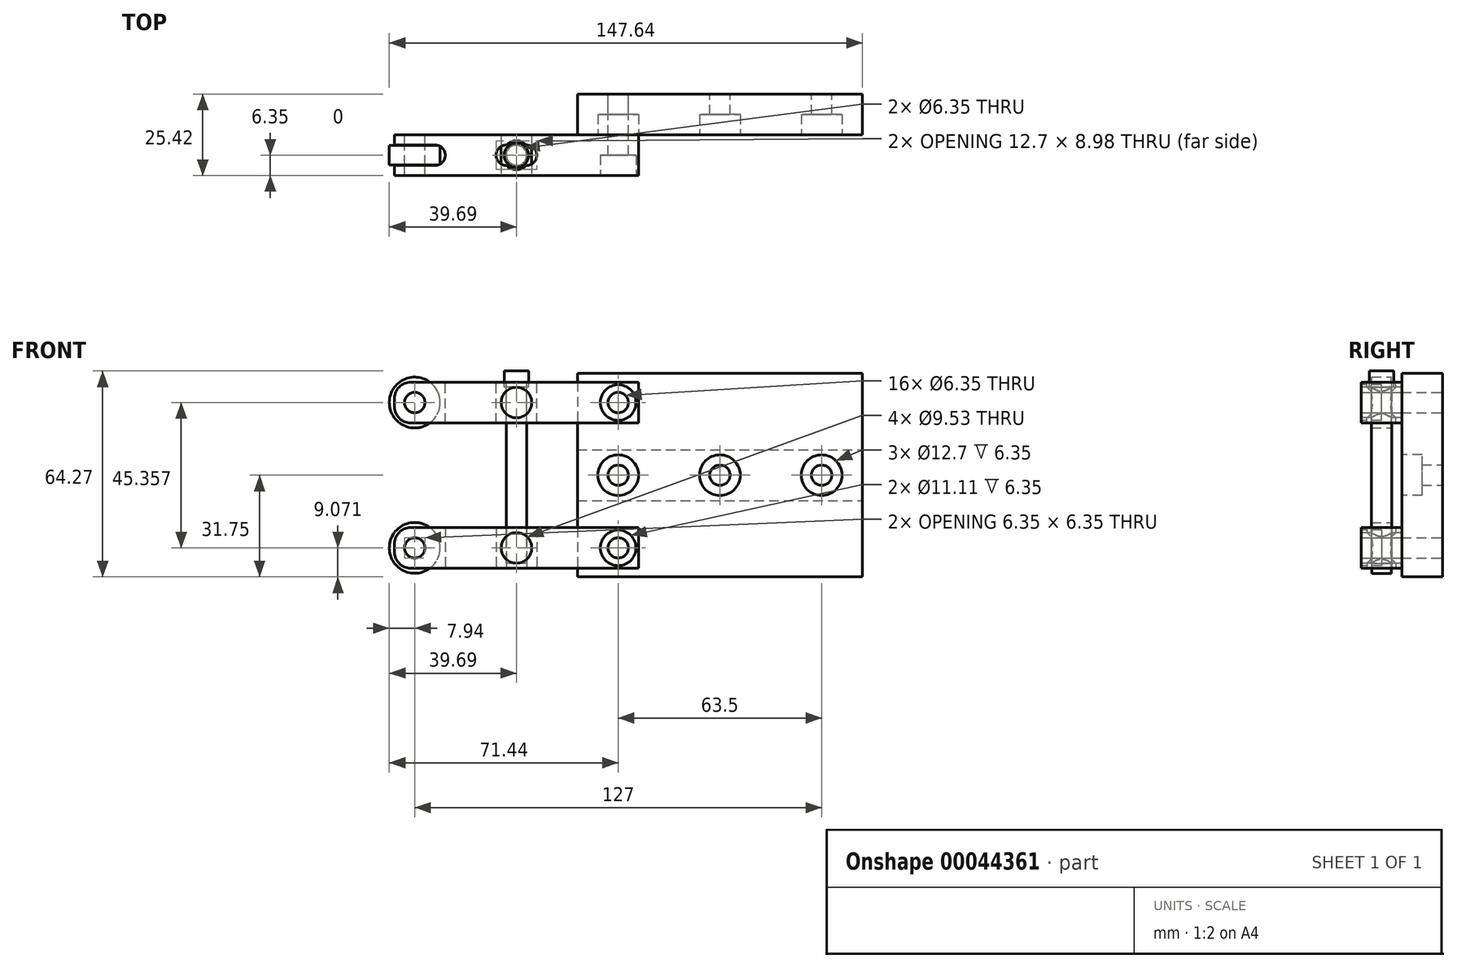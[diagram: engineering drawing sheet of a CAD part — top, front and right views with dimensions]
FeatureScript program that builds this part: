
annotation { "Feature Type Name" : "Feature", "Feature Type Description" : "" }
export const myFeature = defineFeature(function(context is Context, id is Id, definition is map)
    precondition{}
    {
        {
            var Q0;
            Q0=qCreatedBy(makeId("Front.planeOp"),FACE);
            var sketch = newSketch(context, id + "F0", { "sketchPlane" : qUnion([Q0])});
            skLineSegment(sketch, "E0.rect.bottom", {"start": v(44.45, 31.75) * mm, "end": v(-44.45, 31.75) * mm});
            skLineSegment(sketch, "E0.rect.top", {"start": v(44.45, -31.75) * mm, "end": v(-44.45, -31.75) * mm});
            skLineSegment(sketch, "E0.rect.left", {"start": v(44.45, 31.75) * mm, "end": v(44.45, -31.75) * mm});
            skLineSegment(sketch, "E0.rect.right", {"start": v(-44.45, 31.75) * mm, "end": v(-44.45, -31.75) * mm});
            skPoint(sketch, "E0.rect.middle", {"position": v(0, 0) * mm});
            skLineSegment(sketch, "E1", {"start": v(-44.45, 31.75) * mm, "end": v(44.45, -31.75) * mm, "construction": true});
            skLineSegment(sketch, "E2", {"start": v(-44.45, -31.75) * mm, "end": v(-44.45, -31.75) * mm});
            skLineSegment(sketch, "E3", {"start": v(44.45, 31.75) * mm, "end": v(-44.45, -31.75) * mm, "construction": true});
            skLineSegment(sketch, "E4", {"start": v(0, 31.75) * mm, "end": v(0, 0) * mm, "construction": true});
            skLineSegment(sketch, "E5.rect.bottom", {"start": v(31.75, 22.68) * mm, "end": v(-31.75, 22.68) * mm, "construction": true});
            skLineSegment(sketch, "E5.rect.top", {"start": v(31.75, -22.68) * mm, "end": v(-31.75, -22.68) * mm, "construction": true});
            skLineSegment(sketch, "E5.rect.left", {"start": v(31.75, 22.68) * mm, "end": v(31.75, -22.68) * mm, "construction": true});
            skLineSegment(sketch, "E5.rect.right", {"start": v(-31.75, 22.68) * mm, "end": v(-31.75, -22.68) * mm, "construction": true});
            skCircle(sketch, "E6", {"center": v(-31.75, 22.68) * mm, "radius": 3.18 * mm});
            skCircle(sketch, "E7", {"center": v(-31.75, -22.68) * mm, "radius": 3.18 * mm});
            skLineSegment(sketch, "E8", {"start": v(44.45, 0) * mm, "end": v(-44.45, 0) * mm, "construction": true});
            skCircle(sketch, "E9", {"center": v(0, 0) * mm, "radius": 3.18 * mm});
            skCircle(sketch, "E10", {"center": v(-31.75, 0) * mm, "radius": 3.18 * mm});
            skCircle(sketch, "E11", {"center": v(31.75, 0) * mm, "radius": 3.18 * mm});
            skSolve(sketch);
        }
        {
            var Q0;
            Q0 = qSketchRegion(id + "F0", true);
            extrude(context, id + "F1", {"entities" : qUnion([Q0]), "endBound" : BoundingType.SYMMETRIC, "depth" : 12.7 * mm});
        }
        {
            var Q0;
            Q0=makeQuery(id+"F1.opExtrude","CAP_FACE",FACE,{"disambiguationData":[OSD([sQuery(id+"F0.wireOp",EDGE,"E0.rect.bottom"),sQuery(id+"F0.wireOp",EDGE,"E0.rect.top"),sQuery(id+"F0.wireOp",EDGE,"E0.rect.left"),sQuery(id+"F0.wireOp",EDGE,"E0.rect.right"),sQuery(id+"F0.wireOp",EDGE,"E6"),sQuery(id+"F0.wireOp",EDGE,"E7"),sQuery(id+"F0.wireOp",EDGE,"E9"),sQuery(id+"F0.wireOp",EDGE,"E10"),sQuery(id+"F0.wireOp",EDGE,"E11")])],"isStart":true});
            var sketch = newSketch(context, id + "F2", { "sketchPlane" : qUnion([Q0])});
            skLineSegment(sketch, "E12.rect.bottom", {"start": v(44.45, 7.94) * mm, "end": v(-44.45, 7.94) * mm});
            skLineSegment(sketch, "E12.rect.top", {"start": v(44.45, -7.94) * mm, "end": v(-44.45, -7.94) * mm});
            skLineSegment(sketch, "E12.rect.left", {"start": v(44.45, 7.94) * mm, "end": v(44.45, -7.94) * mm});
            skLineSegment(sketch, "E12.rect.right", {"start": v(-44.45, 7.94) * mm, "end": v(-44.45, -7.94) * mm});
            skPoint(sketch, "E12.rect.middle", {"position": v(0, 0) * mm});
            skCircle(sketch, "E13", {"center": v(-31.75, 0) * mm, "radius": 3.18 * mm});
            skCircle(sketch, "E14", {"center": v(0, 0) * mm, "radius": 3.18 * mm});
            skCircle(sketch, "E15", {"center": v(31.75, 0) * mm, "radius": 3.18 * mm});
            skSolve(sketch);
        }
        {
            var Q0;
            Q0 = qSketchRegion(id + "F2", true);
            extrude(context, id + "F3", {"entities" : qUnion([Q0]), "depth" : 5 / 203.2 * mm});
        }
        {
            var Q0;
            Q0=makeQuery(id+"F1.opExtrude","CAP_FACE",FACE,{"disambiguationData":[OSD([sQuery(id+"F0.wireOp",EDGE,"E0.rect.bottom"),sQuery(id+"F0.wireOp",EDGE,"E0.rect.top"),sQuery(id+"F0.wireOp",EDGE,"E0.rect.left"),sQuery(id+"F0.wireOp",EDGE,"E0.rect.right"),sQuery(id+"F0.wireOp",EDGE,"E6"),sQuery(id+"F0.wireOp",EDGE,"E7"),sQuery(id+"F0.wireOp",EDGE,"E9"),sQuery(id+"F0.wireOp",EDGE,"E10"),sQuery(id+"F0.wireOp",EDGE,"E11")])],"isStart":false});
            var sketch = newSketch(context, id + "F15", { "sketchPlane" : qUnion([Q0])});
            skCircle(sketch, "E16", {"center": v(-31.75, 0) * mm, "radius": 6.35 * mm});
            skCircle(sketch, "E17", {"center": v(0, 0) * mm, "radius": 6.35 * mm});
            skCircle(sketch, "E18", {"center": v(31.75, 0) * mm, "radius": 6.35 * mm});
            skSolve(sketch);
        }
        {
            var Q0;
            Q0 = qSketchRegion(id + "F15", true);
            extrude(context, id + "F4", {"entities" : qUnion([Q0]), "operationType" : NewBodyOperationType.REMOVE, "oppositeDirection" : true, "depth" : 6.35 * mm});
        }
        {
            var Q0;
            Q0=makeQuery(id+"F1.opExtrude","CAP_FACE",FACE,{"disambiguationData":[OSD([sQuery(id+"F0.wireOp",EDGE,"E0.rect.bottom"),sQuery(id+"F0.wireOp",EDGE,"E0.rect.top"),sQuery(id+"F0.wireOp",EDGE,"E0.rect.left"),sQuery(id+"F0.wireOp",EDGE,"E0.rect.right"),sQuery(id+"F0.wireOp",EDGE,"E6"),sQuery(id+"F0.wireOp",EDGE,"E7"),sQuery(id+"F0.wireOp",EDGE,"E9"),sQuery(id+"F0.wireOp",EDGE,"E10"),sQuery(id+"F0.wireOp",EDGE,"E11")])],"isStart":false});
            var sketch = newSketch(context, id + "F16", { "sketchPlane" : qUnion([Q0])});
            skPoint(sketch, "E19", {"position": v(-31.75, 22.68) * mm});
            skLineSegment(sketch, "E20.rect.bottom", {"start": v(-25.4, 16.33) * mm, "end": v(-101.6, 16.33) * mm});
            skLineSegment(sketch, "E20.rect.top", {"start": v(-25.4, 29.03) * mm, "end": v(-101.6, 29.03) * mm});
            skLineSegment(sketch, "E20.rect.left", {"start": v(-25.4, 16.33) * mm, "end": v(-25.4, 29.03) * mm});
            skLineSegment(sketch, "E20.rect.right", {"start": v(-101.6, 16.33) * mm, "end": v(-101.6, 29.03) * mm});
            skPoint(sketch, "E20.rect.middle", {"position": v(-63.5, 22.68) * mm});
            skLineSegment(sketch, "E21", {"start": v(-95.25, 22.68) * mm, "end": v(-31.75, 22.68) * mm, "construction": true});
            skLineSegment(sketch, "E22", {"start": v(-25.4, 29.03) * mm, "end": v(-38.1, 16.33) * mm, "construction": true});
            skLineSegment(sketch, "E23", {"start": v(-25.4, 16.33) * mm, "end": v(-38.1, 29.03) * mm, "construction": true});
            skCircle(sketch, "E24", {"center": v(-31.75, 22.68) * mm, "radius": 3.18 * mm});
            skCircle(sketch, "E25", {"center": v(-95.25, 22.68) * mm, "radius": 3.18 * mm});
            skLineSegment(sketch, "E26", {"start": v(-31.75, 0) * mm, "end": v(31.75, 0) * mm, "construction": true});
            skPoint(sketch, "E27", {"position": v(31.75, 0) * mm});
            skLineSegment(sketch, "E28.MirrorCS", {"start": v(-101.6, -16.33) * mm, "end": v(-101.6, -29.03) * mm, "construction": true});
            skCircle(sketch, "E29.MirrorC", {"center": v(-95.25, -22.68) * mm, "radius": 3.18 * mm, "construction": true});
            skCircle(sketch, "E30.MirrorC", {"center": v(-31.75, -22.68) * mm, "radius": 3.18 * mm, "construction": true});
            skLineSegment(sketch, "E31.MirrorCS", {"start": v(-25.4, -16.33) * mm, "end": v(-25.4, -29.03) * mm, "construction": true});
            skPoint(sketch, "E32.MirrorCS.end.orphan", {"position": v(-101.6, -29.03) * mm});
            skPoint(sketch, "E32.MirrorCS.start.orphan", {"position": v(-25.4, -29.03) * mm});
            skLineSegment(sketch, "E33.MirrorCS", {"start": v(-25.4, -16.33) * mm, "end": v(-101.6, -16.33) * mm, "construction": true});
            skLineSegment(sketch, "E34.MirrorCS", {"start": v(-25.4, -29.03) * mm, "end": v(-101.6, -29.03) * mm, "construction": true});
            skSolve(sketch);
        }
        {
            var Q0;
            Q0 = qSketchRegion(id + "F16", true);
            extrude(context, id + "F17", {"entities" : qUnion([Q0]), "depth" : 12.7 * mm});
        }
        {
            var Q0;
            Q0=makeQuery(id+"F17.opExtrude","CAP_FACE",FACE,{"disambiguationData":[OSD([sQuery(id+"F16.wireOp",EDGE,"E20.rect.bottom"),sQuery(id+"F16.wireOp",EDGE,"E20.rect.top"),sQuery(id+"F16.wireOp",EDGE,"E20.rect.left"),sQuery(id+"F16.wireOp",EDGE,"E20.rect.right"),sQuery(id+"F16.wireOp",EDGE,"E24"),sQuery(id+"F16.wireOp",EDGE,"E25")])],"isStart":false});
            var sketch = newSketch(context, id + "F5", { "sketchPlane" : qUnion([Q0])});
            skLineSegment(sketch, "E35", {"start": v(-31.75, 22.68) * mm, "end": v(-95.25, 22.68) * mm, "construction": true});
            skCircle(sketch, "E36", {"center": v(-31.75, 22.68) * mm, "radius": 5.56 * mm});
            skSolve(sketch);
        }
        {
            var Q0;
            Q0 = qSketchRegion(id + "F5", true);
            extrude(context, id + "F18", {"entities" : qUnion([Q0]), "operationType" : NewBodyOperationType.REMOVE, "oppositeDirection" : true, "depth" : 6.35 * mm});
        }
        {
            var Q0;
            Q0=makeQuery(id+"F17.opExtrude","CAP_FACE",FACE,{"disambiguationData":[OSD([sQuery(id+"F16.wireOp",EDGE,"E20.rect.bottom"),sQuery(id+"F16.wireOp",EDGE,"E20.rect.top"),sQuery(id+"F16.wireOp",EDGE,"E20.rect.left"),sQuery(id+"F16.wireOp",EDGE,"E20.rect.right"),sQuery(id+"F16.wireOp",EDGE,"E24"),sQuery(id+"F16.wireOp",EDGE,"E25")])],"isStart":false});
            var sketch = newSketch(context, id + "F6", { "sketchPlane" : qUnion([Q0])});
            skCircle(sketch, "E37", {"center": v(-63.5, 22.68) * mm, "radius": 4.76 * mm});
            skLineSegment(sketch, "E38", {"start": v(-95.25, 22.68) * mm, "end": v(-31.75, 22.68) * mm, "construction": true});
            skSolve(sketch);
        }
        {
            var Q0;
            Q0 = qSketchRegion(id + "F6", true);
            extrude(context, id + "F7", {"entities" : qUnion([Q0]), "operationType" : NewBodyOperationType.REMOVE, "endBound" : BoundingType.UP_TO_NEXT, "oppositeDirection" : true, "depth" : 25.4 * mm});
        }
        {
            var Q0;
            Q0=makeQuery(id+"F17.opExtrude","SWEPT_FACE",FACE,{"disambiguationData":[OSD([sQuery(id+"F16.wireOp",EDGE,"E20.rect.top")])]});
            var sketch = newSketch(context, id + "F8", { "sketchPlane" : qUnion([Q0])});
            skCircle(sketch, "E39", {"center": v(-63.5, -12.7) * mm, "radius": 3.18 * mm, "construction": true});
            skLineSegment(sketch, "E40", {"start": v(-101.6, -12.7) * mm, "end": v(-25.4, -12.7) * mm, "construction": true});
            skArc(sketch, "E41", {"start": v(-88.9, -15.88) * mm, "mid": v(-85.73, -12.7) * mm, "end": v(-88.9, -9.53) * mm});
            skLineSegment(sketch, "E42", {"start": v(-88.9, -9.53) * mm, "end": v(-101.6, -9.53) * mm});
            skLineSegment(sketch, "E43", {"start": v(-88.9, -15.88) * mm, "end": v(-101.6, -15.88) * mm});
            skLineSegment(sketch, "E44", {"start": v(-101.6, -9.53) * mm, "end": v(-101.6, -15.88) * mm});
            skLineSegment(sketch, "E45", {"start": v(-66.67, -12.7) * mm, "end": v(-60.33, -12.7) * mm, "construction": true});
            skArc(sketch, "E46.0.startCap", {"start": v(-66.67, -15.88) * mm, "mid": v(-69.85, -12.7) * mm, "end": v(-66.67, -9.53) * mm});
            skArc(sketch, "E46.0.endCap", {"start": v(-60.33, -9.53) * mm, "mid": v(-57.15, -12.7) * mm, "end": v(-60.33, -15.88) * mm});
            skLineSegment(sketch, "E46.0.left", {"start": v(-66.67, -9.53) * mm, "end": v(-60.33, -9.53) * mm, "construction": true});
            skLineSegment(sketch, "E46.0.right", {"start": v(-66.67, -15.88) * mm, "end": v(-60.33, -15.88) * mm, "construction": true});
            skArc(sketch, "E47", {"start": v(-60.32, -9.53) * mm, "mid": v(-63.5, -8.2) * mm, "end": v(-66.67, -9.53) * mm});
            skArc(sketch, "E48.trimOffspring", {"start": v(-66.67, -15.88) * mm, "mid": v(-63.5, -17.2) * mm, "end": v(-60.33, -15.88) * mm});
            skSolve(sketch);
        }
        {
            var Q0;
            Q0 = qSketchRegion(id + "F8", true);
            extrude(context, id + "F9", {"entities" : qUnion([Q0]), "operationType" : NewBodyOperationType.REMOVE, "endBound" : BoundingType.THROUGH_ALL, "oppositeDirection" : true, "depth" : 25.4 * mm});
        }
        {
            var Q0;
            Q0=makeQuery(id+"F17.opExtrude","CAP_FACE",FACE,{"disambiguationData":[OSD([sQuery(id+"F16.wireOp",EDGE,"E20.rect.bottom"),sQuery(id+"F16.wireOp",EDGE,"E20.rect.top"),sQuery(id+"F16.wireOp",EDGE,"E20.rect.left"),sQuery(id+"F16.wireOp",EDGE,"E20.rect.right"),sQuery(id+"F16.wireOp",EDGE,"E24"),sQuery(id+"F16.wireOp",EDGE,"E25")])],"isStart":false});
            var sketch = newSketch(context, id + "F19", { "sketchPlane" : qUnion([Q0])});
            skLineSegment(sketch, "E49.0", {"start": v(44.45, -31.75) * mm, "end": v(-44.45, -31.75) * mm});
            skCircle(sketch, "E49.1", {"center": v(-63.5, 22.68) * mm, "radius": 4.76 * mm});
            skCircle(sketch, "E50.0", {"center": v(-95.25, 22.68) * mm, "radius": 3.18 * mm, "construction": true});
            skCircle(sketch, "E51.0", {"center": v(-31.75, 22.68) * mm, "radius": 3.18 * mm, "construction": true});
            skLineSegment(sketch, "E52", {"start": v(-95.25, 22.68) * mm, "end": v(-63.5, 22.68) * mm, "construction": true});
            skSolve(sketch);
        }
        {
            var Q0;
            Q0=makeQuery(id+"F17.opExtrude","SWEPT_FACE",FACE,{"disambiguationData":[OSD([sQuery(id+"F16.wireOp",EDGE,"E20.rect.top")])]});
            var sketch = newSketch(context, id + "F10", { "sketchPlane" : qUnion([Q0])});
            skLineSegment(sketch, "E53", {"start": v(-69.85, -12.7) * mm, "end": v(-57.15, -12.7) * mm, "construction": true});
            skCircle(sketch, "E54", {"center": v(-63.5, -12.7) * mm, "radius": 3.17 * mm});
            skLineSegment(sketch, "E55", {"start": v(-66.67, -9.53) * mm, "end": v(-60.32, -9.53) * mm, "construction": true});
            skLineSegment(sketch, "E56", {"start": v(-60.32, -9.53) * mm, "end": v(-60.32, -9.53) * mm});
            skSolve(sketch);
        }
        {
            var Q0;
            Q0=makeQuery(id+"F9.boolean.opBoolean","COPY",FACE,{"derivedFrom":makeQuery(id+"F9.opExtrude","SWEPT_FACE",FACE,{"disambiguationData":[OSD([sQuery(id+"F8.wireOp",EDGE,"E42")])]})});
            var Q1;
            Q1=makeQuery(id+"F9.boolean.opBoolean","COPY",FACE,{"derivedFrom":makeQuery(id+"F9.opExtrude","SWEPT_FACE",FACE,{"disambiguationData":[OSD([sQuery(id+"F8.wireOp",EDGE,"E43")])]})});
            cPlane(context, id + "F11", {"entities" : qUnion([Q0, Q1]), "cplaneType" : CPlaneType.MID_PLANE, "offset" : 152.4 * mm, "width" : 152.4 * mm, "height" : 152.4 * mm});
        }
        {
            var Q0;
            Q0=qCreatedBy(id+"F11.planeOp",FACE);
            var sketch = newSketch(context, id + "F12", { "sketchPlane" : qUnion([Q0])});
            skCircle(sketch, "E57.0", {"center": v(-95.25, 22.68) * mm, "radius": 3.18 * mm});
            skCircle(sketch, "E58", {"center": v(-95.25, 22.68) * mm, "radius": 7.94 * mm});
            skSolve(sketch);
        }
        {
            var Q0;
            Q0 = qSketchRegion(id + "F12", true);
            extrude(context, id + "F20", {"entities" : qUnion([Q0]), "endBound" : BoundingType.SYMMETRIC, "depth" : 6.1 * mm});
        }
        {
            var Q0;
            {var subQ0=sQuery(id+"F16.wireOp",EDGE,"E20.rect.top");var subQ1=sQuery(id+"F16.wireOp",EDGE,"E20.rect.right");Q0=makeQuery(id+"F9.boolean.opBoolean","SPLIT",EDGE,{"disambiguationData":[TD([makeQuery(id+"F9.opExtrude","SWEPT_FACE",FACE,{"disambiguationData":[OSD([sQuery(id+"F8.wireOp",EDGE,"E43")])]})])],"derivedFrom":makeQuery(id+"F17.opExtrude","SWEPT_EDGE",EDGE,{"disambiguationData":[OSD([subQ0,subQ1])]})});}
            var Q1;
            {var subQ0=sQuery(id+"F16.wireOp",EDGE,"E20.rect.top");var subQ1=sQuery(id+"F16.wireOp",EDGE,"E20.rect.right");Q1=makeQuery(id+"F9.boolean.opBoolean","SPLIT",EDGE,{"disambiguationData":[TD([makeQuery(id+"F9.opExtrude","SWEPT_FACE",FACE,{"disambiguationData":[OSD([sQuery(id+"F8.wireOp",EDGE,"E42")])]})])],"derivedFrom":makeQuery(id+"F17.opExtrude","SWEPT_EDGE",EDGE,{"disambiguationData":[OSD([subQ0,subQ1])]})});}
            var Q2;
            {var subQ0=sQuery(id+"F16.wireOp",EDGE,"E20.rect.bottom");var subQ1=sQuery(id+"F16.wireOp",EDGE,"E20.rect.right");Q2=makeQuery(id+"F9.boolean.opBoolean","SPLIT",EDGE,{"disambiguationData":[TD([makeQuery(id+"F9.opExtrude","SWEPT_FACE",FACE,{"disambiguationData":[OSD([sQuery(id+"F8.wireOp",EDGE,"E43")])]})])],"derivedFrom":makeQuery(id+"F17.opExtrude","SWEPT_EDGE",EDGE,{"disambiguationData":[OSD([subQ0,subQ1])]})});}
            var Q3;
            {var subQ0=sQuery(id+"F16.wireOp",EDGE,"E20.rect.bottom");var subQ1=sQuery(id+"F16.wireOp",EDGE,"E20.rect.right");Q3=makeQuery(id+"F9.boolean.opBoolean","SPLIT",EDGE,{"disambiguationData":[TD([makeQuery(id+"F9.opExtrude","SWEPT_FACE",FACE,{"disambiguationData":[OSD([sQuery(id+"F8.wireOp",EDGE,"E42")])]})])],"derivedFrom":makeQuery(id+"F17.opExtrude","SWEPT_EDGE",EDGE,{"disambiguationData":[OSD([subQ0,subQ1])]})});}
            fillet(context, id + "F21", {"entities" : qUnion([Q0, Q1, Q2, Q3]), "radius" : 5.08 * mm, "tangentPropagation" : true, "allowEdgeOverflow" : false});
        }
        {
            var Q0;
            Q0=makeQuery(id+"F19.imprint","IMPRINT",FACE,{"disambiguationData":[TD([[makeQuery(id+"F19.imprint","IMPRINT",EDGE,{"derivedFrom":sQuery(id+"F19.wireOp",EDGE,"E49.1")}),1.0]])]});
            var Q1;
            Q1 = qBodyType(qCreatedBy(id + "F19" ,EDGE), BodyType.WIRE);
            var Q2;
            Q2=makeQuery(id+"F17.opExtrude","CAP_FACE",FACE,{"disambiguationData":[OSD([sQuery(id+"F16.wireOp",EDGE,"E20.rect.bottom"),sQuery(id+"F16.wireOp",EDGE,"E20.rect.top"),sQuery(id+"F16.wireOp",EDGE,"E20.rect.left"),sQuery(id+"F16.wireOp",EDGE,"E20.rect.right"),sQuery(id+"F16.wireOp",EDGE,"E24"),sQuery(id+"F16.wireOp",EDGE,"E25")])],"isStart":true});
            extrude(context, id + "F22", {"entities" : qUnion([Q0]), "surfaceEntities" : qUnion([Q1]), "endBound" : BoundingType.UP_TO_SURFACE, "oppositeDirection" : true, "endBoundEntityFace" : qUnion([Q2]), "depth" : 25.4 * mm});
        }
        {
            var Q0;
            {var subQ0=sQuery(id+"F16.wireOp",EDGE,"E20.rect.top");Q0=makeQuery(id+"F10.imprint","IMPRINT",FACE,{"disambiguationData":[TD([[makeQuery(id+"F10.imprint","IMPRINT",EDGE,{"derivedFrom":makeQuery(id+"F17.opExtrude","CAP_EDGE",EDGE,{"disambiguationData":[OSD([subQ0])],"isStart":true})}),1.0]])]});}
            var sketch = newSketch(context, id + "F13", { "sketchPlane" : qUnion([Q0])});
            skCircle(sketch, "E59.0", {"center": v(-63.5, -12.7) * mm, "radius": 3.17 * mm});
            skSolve(sketch);
        }
        {
            var Q0;
            Q0 = qSketchRegion(id + "F13", true);
            extrude(context, id + "F14", {"entities" : qUnion([Q0]), "operationType" : NewBodyOperationType.REMOVE, "endBound" : BoundingType.THROUGH_ALL, "oppositeDirection" : true, "depth" : 25.4 * mm});
        }
        {
            var Q0;
            Q0=makeQuery(id+"F20.opExtrude","SWEPT_BODY",BODY,{"disambiguationData":[OSD([sQuery(id+"F12.wireOp",EDGE,"E57.0"),sQuery(id+"F12.wireOp",EDGE,"E58")])]});
            var Q1;
            Q1=makeQuery(id+"F17.opExtrude","SWEPT_BODY",BODY,{"disambiguationData":[OSD([sQuery(id+"F16.wireOp",EDGE,"E20.rect.bottom"),sQuery(id+"F16.wireOp",EDGE,"E20.rect.top"),sQuery(id+"F16.wireOp",EDGE,"E20.rect.left"),sQuery(id+"F16.wireOp",EDGE,"E20.rect.right"),sQuery(id+"F16.wireOp",EDGE,"E24"),sQuery(id+"F16.wireOp",EDGE,"E25")])]});
            var Q2;
            Q2=makeQuery(id+"F22.opExtrude","SWEPT_BODY",BODY,{"disambiguationData":[OSD([sQuery(id+"F19.wireOp",EDGE,"E49.1")])]});
            var Q3;
            Q3=qCreatedBy(makeId("Top.planeOp"),FACE);
            mirror(context, id + "F23", {"entities" : qUnion([Q0, Q1, Q2]), "mirrorPlane" : qUnion([Q3])});
        }
        {
            var Q0;
            Q0=qCreatedBy(id+"F11.planeOp",FACE);
            var sketch = newSketch(context, id + "F24", { "sketchPlane" : qUnion([Q0])});
            skLineSegment(sketch, "E60", {"start": v(-63.5, 22.68) * mm, "end": v(-63.5, -22.68) * mm, "construction": true});
            skCircle(sketch, "E61.0", {"center": v(-63.5, 22.68) * mm, "radius": 4.76 * mm, "construction": true});
            skCircle(sketch, "E62.0", {"center": v(-63.5, -22.68) * mm, "radius": 4.76 * mm, "construction": true});
            skLineSegment(sketch, "E63", {"start": v(-63.5, 32.52) * mm, "end": v(-63.5, -27.44) * mm});
            skLineSegment(sketch, "E64", {"start": v(-63.5, 32.52) * mm, "end": v(-59.69, 32.52) * mm});
            skLineSegment(sketch, "E65", {"start": v(-59.69, 32.52) * mm, "end": v(-59.69, 27.44) * mm});
            skLineSegment(sketch, "E66", {"start": v(-59.69, 27.44) * mm, "end": v(-60.32, 27.44) * mm});
            skLineSegment(sketch, "E67", {"start": v(-60.32, 27.44) * mm, "end": v(-60.32, -27.44) * mm});
            skLineSegment(sketch, "E68", {"start": v(-60.32, -27.44) * mm, "end": v(-63.5, -27.44) * mm});
            skLineSegment(sketch, "E69", {"start": v(-60.32, 27.44) * mm, "end": v(-63.5, 27.44) * mm, "construction": true});
            skSolve(sketch);
        }
        {
            var Q0;
            Q0=makeQuery(id+"F24.imprint","IMPRINT",FACE,{"disambiguationData":[TD([[makeQuery(id+"F24.imprint","IMPRINT",EDGE,{"derivedFrom":sQuery(id+"F24.wireOp",EDGE,"E63")}),1.0]])]});
            var Q1;
            Q1=sQuery(id+"F24.wireOp",EDGE,"E60");
            revolve(context, id + "F25", {"entities" : qUnion([Q0]), "axis" : qUnion([Q1]), "revolveType" : RevolveType.FULL});
        }
    });
